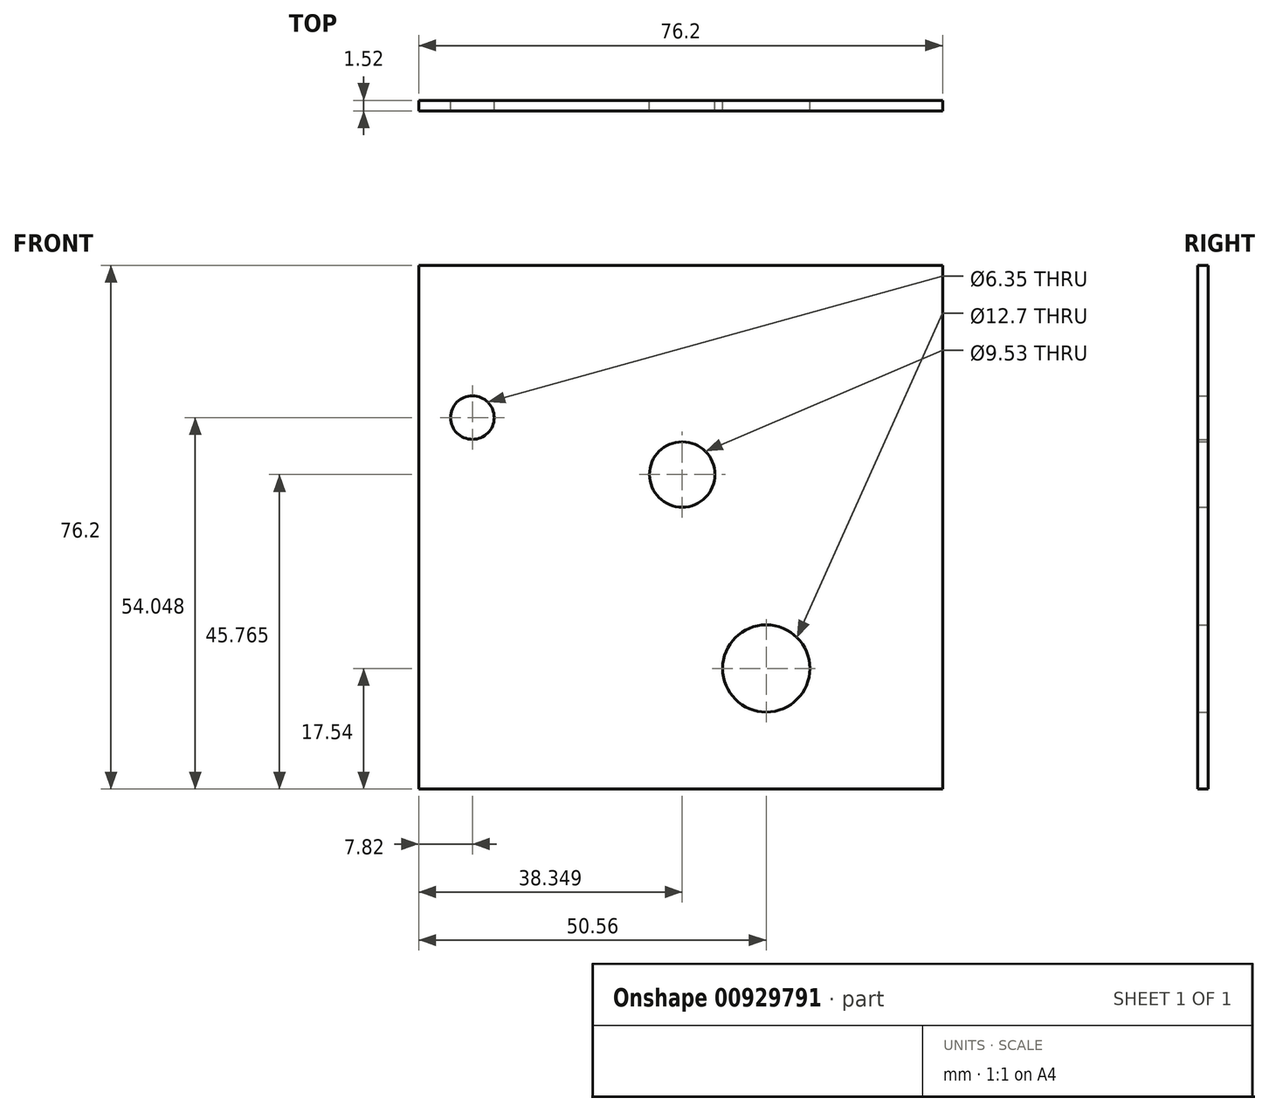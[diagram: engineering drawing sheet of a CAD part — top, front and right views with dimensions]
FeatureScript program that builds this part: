
annotation { "Feature Type Name" : "Feature", "Feature Type Description" : "" }
export const myFeature = defineFeature(function(context is Context, id is Id, definition is map)
    precondition{}
    {
        {
            var Q0;
            Q0=qCreatedBy(makeId("Front.planeOp"),FACE);
            var sketch = newSketch(context, id + "F0", { "sketchPlane" : qUnion([Q0])});
            skLineSegment(sketch, "E0.bottom", {"start": v(-61.82, 55.57) * mm, "end": v(14.38, 55.57) * mm});
            skLineSegment(sketch, "E0.top", {"start": v(-61.82, -20.63) * mm, "end": v(14.38, -20.63) * mm});
            skLineSegment(sketch, "E0.left", {"start": v(-61.82, 55.57) * mm, "end": v(-61.82, -20.63) * mm});
            skLineSegment(sketch, "E0.right", {"start": v(14.38, 55.57) * mm, "end": v(14.38, -20.63) * mm});
            skCircle(sketch, "E1", {"center": v(-54, 33.42) * mm, "radius": 3.17 * mm});
            skCircle(sketch, "E2", {"center": v(-11.26, -3.1) * mm, "radius": 6.35 * mm});
            skCircle(sketch, "E3", {"center": v(-23.47, 25.13) * mm, "radius": 4.76 * mm});
            skSolve(sketch);
        }
        {
            var Q0;
            Q0=makeQuery(id+"F0.imprint","IMPRINT",FACE,{"disambiguationData":[TD([[makeQuery(id+"F0.imprint","IMPRINT",EDGE,{"derivedFrom":sQuery(id+"F0.wireOp",EDGE,"E0.bottom")}),-1.0]])]});
            extrude(context, id + "F1", {"entities" : qUnion([Q0]), "depth" : 1.52 * mm, "offsetDistance" : 25.4 * mm});
        }
    });
